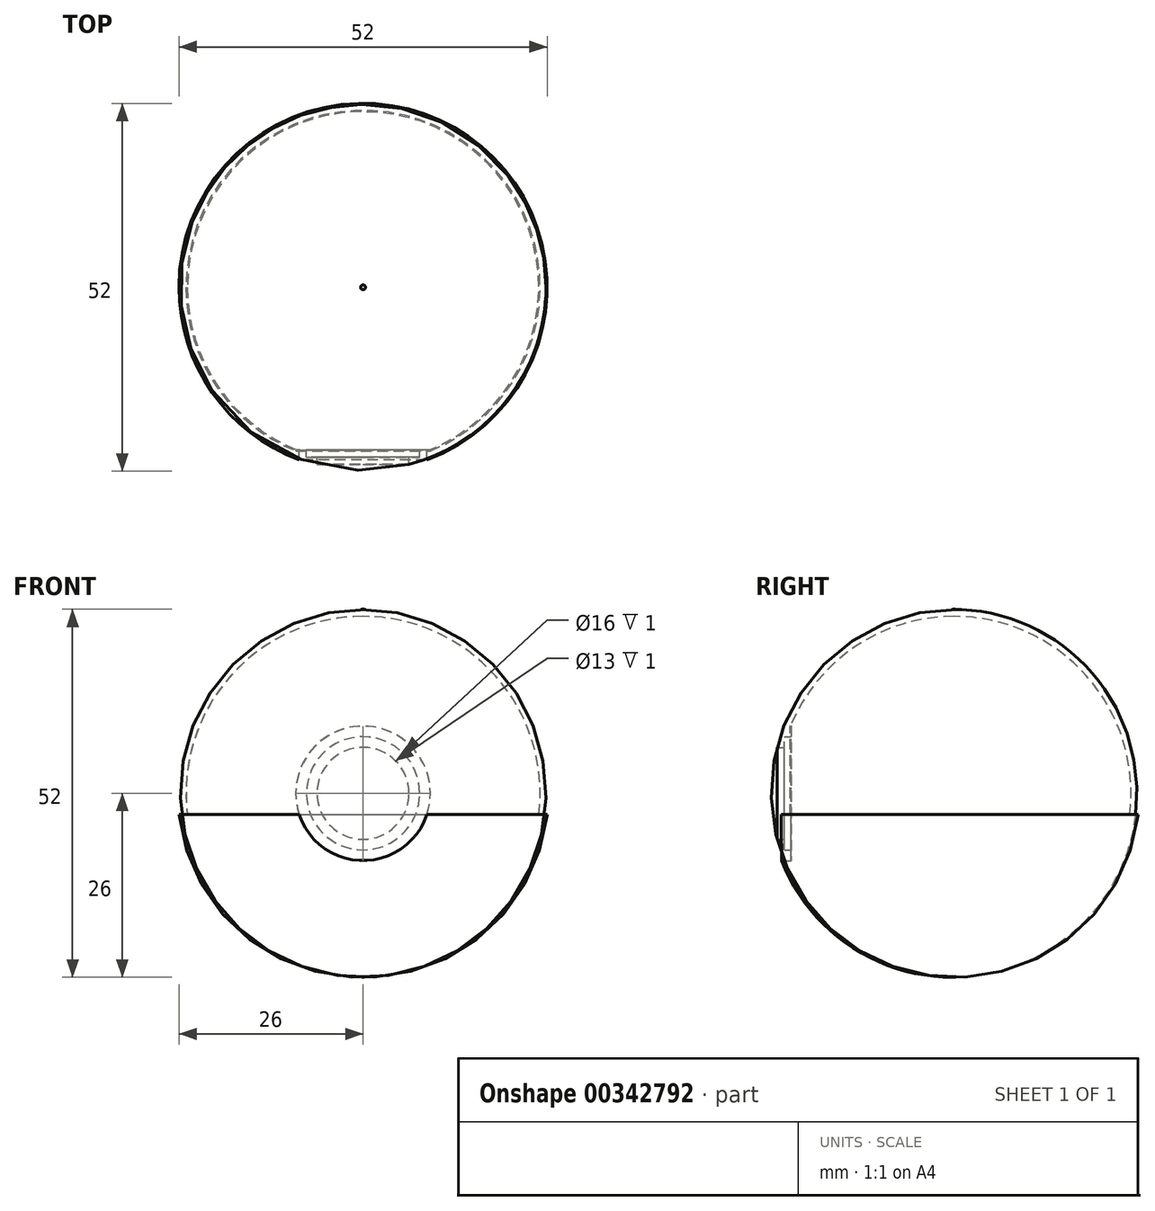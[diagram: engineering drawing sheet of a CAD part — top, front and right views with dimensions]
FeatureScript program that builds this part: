
annotation { "Feature Type Name" : "Feature", "Feature Type Description" : "" }
export const myFeature = defineFeature(function(context is Context, id is Id, definition is map)
    precondition{}
    {
        {
            var Q0;
            Q0=qCreatedBy(makeId("Front.planeOp"),FACE);
            var sketch = newSketch(context, id + "F0", { "sketchPlane" : qUnion([Q0])});
            skLineSegment(sketch, "E0", {"start": v(0, -25) * mm, "end": v(0, 25) * mm});
            skArc(sketch, "E1", {"start": v(0, -25) * mm, "mid": v(25, 0) * mm, "end": v(0, 25) * mm});
            skSolve(sketch);
        }
        {
            var Q0;
            Q0=makeQuery(id+"F0.imprint","IMPRINT",FACE,{"disambiguationData":[TD([[makeQuery(id+"F0.imprint","IMPRINT",EDGE,{"derivedFrom":sQuery(id+"F0.wireOp",EDGE,"E0")}),-1.0]])]});
            var Q1;
            Q1=sQuery(id+"F0.wireOp",EDGE,"E0");
            revolve(context, id + "F1", {"entities" : qUnion([Q0]), "axis" : qUnion([Q1]), "revolveType" : RevolveType.FULL});
        }
        {
            var Q0;
            Q0=qCreatedBy(makeId("Front.planeOp"),FACE);
            var sketch = newSketch(context, id + "F2", { "sketchPlane" : qUnion([Q0])});
            skLineSegment(sketch, "E2", {"start": v(0, -26) * mm, "end": v(0, -3) * mm});
            skLineSegment(sketch, "E3", {"start": v(0, -3) * mm, "end": v(26, -3) * mm});
            skArc(sketch, "E4", {"start": v(0, -26) * mm, "mid": v(17.4, -19.47) * mm, "end": v(26, -3) * mm});
            skSolve(sketch);
        }
        {
            var Q0;
            Q0 = qSketchRegion(id + "F2", true);
            var Q1;
            Q1=sQuery(id+"F2.wireOp",EDGE,"E2");
            revolve(context, id + "F3", {"operationType" : NewBodyOperationType.ADD, "entities" : qUnion([Q0]), "axis" : qUnion([Q1]), "revolveType" : RevolveType.FULL});
        }
        {
            var Q0;
            Q0=qCreatedBy(makeId("Front.planeOp"),FACE);
            cPlane(context, id + "F4", {"entities" : qUnion([Q0]), "cplaneType" : CPlaneType.OFFSET, "offset" : 23 * mm, "width" : 150 * mm, "height" : 150 * mm});
        }
        {
            var Q0;
            Q0=qCreatedBy(id+"F4.planeOp",FACE);
            var sketch = newSketch(context, id + "F5", { "sketchPlane" : qUnion([Q0])});
            skCircle(sketch, "E5", {"center": v(0, 0) * mm, "radius": 9.5 * mm});
            skSolve(sketch);
        }
        {
            var Q0;
            Q0 = qSketchRegion(id + "F5", true);
            extrude(context, id + "F6", {"entities" : qUnion([Q0]), "operationType" : NewBodyOperationType.REMOVE, "oppositeDirection" : true, "depth" : -20 * mm});
        }
        {
            var Q0;
            Q0=qCreatedBy(id+"F4.planeOp",FACE);
            var sketch = newSketch(context, id + "F7", { "sketchPlane" : qUnion([Q0])});
            skCircle(sketch, "E6", {"center": v(0, 0) * mm, "radius": 8 * mm});
            skSolve(sketch);
        }
        {
            var Q0;
            Q0 = qSketchRegion(id + "F7", true);
            extrude(context, id + "F8", {"entities" : qUnion([Q0]), "operationType" : NewBodyOperationType.ADD, "depth" : 1 * mm});
        }
        {
            var Q0;
            Q0=qCreatedBy(id+"F4.planeOp",FACE);
            var sketch = newSketch(context, id + "F9", { "sketchPlane" : qUnion([Q0])});
            skCircle(sketch, "E7", {"center": v(0, 0) * mm, "radius": 6.5 * mm});
            skSolve(sketch);
        }
        {
            var Q0;
            Q0 = qSketchRegion(id + "F9", true);
            extrude(context, id + "F10", {"entities" : qUnion([Q0]), "operationType" : NewBodyOperationType.ADD, "depth" : 2 * mm});
        }
    });
